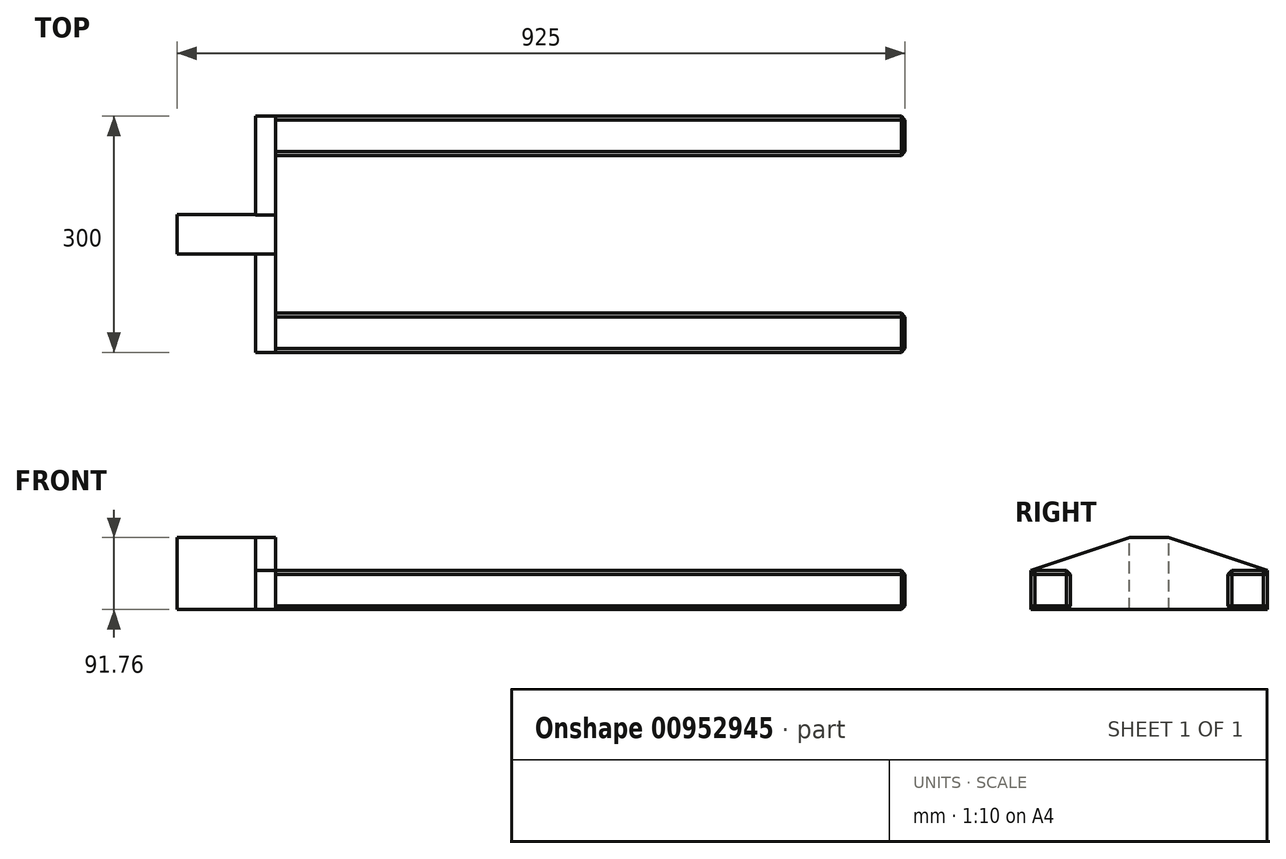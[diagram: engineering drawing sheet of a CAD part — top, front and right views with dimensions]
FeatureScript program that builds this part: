
annotation { "Feature Type Name" : "Feature", "Feature Type Description" : "" }
export const myFeature = defineFeature(function(context is Context, id is Id, definition is map)
    precondition{}
    {
        {
            var Q0;
            Q0=qCreatedBy(makeId("Top.planeOp"),FACE);
            var sketch = newSketch(context, id + "F0", { "sketchPlane" : qUnion([Q0])});
            skLineSegment(sketch, "E0.bottom", {"start": v(0, -100) * mm, "end": v(800, -100) * mm});
            skLineSegment(sketch, "E0.top", {"start": v(0, -150) * mm, "end": v(800, -150) * mm});
            skLineSegment(sketch, "E0.left", {"start": v(0, -100) * mm, "end": v(0, -150) * mm});
            skLineSegment(sketch, "E0.right", {"start": v(800, -100) * mm, "end": v(800, -150) * mm});
            skLineSegment(sketch, "E1.MirrorCS", {"start": v(0, 100) * mm, "end": v(800, 100) * mm});
            skLineSegment(sketch, "E2.MirrorCS", {"start": v(0, 100) * mm, "end": v(0, 150) * mm});
            skLineSegment(sketch, "E3.MirrorCS", {"start": v(0, 150) * mm, "end": v(800, 150) * mm});
            skLineSegment(sketch, "E4.MirrorCS", {"start": v(800, 100) * mm, "end": v(800, 150) * mm});
            skSolve(sketch);
        }
        {
            var Q0;
            Q0 = qSketchRegion(id + "F0", true);
            extrude(context, id + "F1", {"entities" : qUnion([Q0]), "depth" : 50 * mm, "offsetDistance" : 25 * mm});
        }
        {
            var Q0;
            Q0=makeQuery(id+"F1.opExtrude","SWEPT_FACE",FACE,{"disambiguationData":[OSD([sQuery(id+"F0.wireOp",EDGE,"E2.MirrorCS")])]});
            var sketch = newSketch(context, id + "F2", { "sketchPlane" : qUnion([Q0])});
            skLineSegment(sketch, "E5", {"start": v(0, 0) * mm, "end": v(-150, 0) * mm});
            skLineSegment(sketch, "E6", {"start": v(-150, 0) * mm, "end": v(-150, 50) * mm});
            skLineSegment(sketch, "E7", {"start": v(-150, 50) * mm, "end": v(-24.72, 91.76) * mm});
            skLineSegment(sketch, "E8", {"start": v(-24.72, 91.76) * mm, "end": v(0, 91.76) * mm});
            skLineSegment(sketch, "E9.MirrorCS", {"start": v(24.72, 91.76) * mm, "end": v(0, 91.76) * mm});
            skLineSegment(sketch, "E10.MirrorCS", {"start": v(150, 50) * mm, "end": v(24.72, 91.76) * mm});
            skLineSegment(sketch, "E11.MirrorCS", {"start": v(150, 0) * mm, "end": v(150, 50) * mm});
            skLineSegment(sketch, "E12.MirrorCS", {"start": v(0, 0) * mm, "end": v(150, 0) * mm});
            skSolve(sketch);
        }
        {
            var Q0;
            Q0=makeQuery(id+"F2.imprint","IMPRINT",FACE,{"disambiguationData":[TD([[makeQuery(id+"F2.imprint","IMPRINT",EDGE,{"derivedFrom":sQuery(id+"F2.wireOp",EDGE,"E7")}),-1.0]])]});
            var Q1;
            {var subQ3=sQuery(id+"F2.wireOp",EDGE,"E6");Q1=makeQuery(id+"F2.imprint","IMPRINT",FACE,{"disambiguationData":[TD([[makeQuery(id+"F2.imprint","IMPRINT",EDGE,{"derivedFrom":subQ3}),1.0]])]});}
            extrude(context, id + "F3", {"entities" : qUnion([Q0, Q1]), "depth" : 25 * mm, "offsetDistance" : 25 * mm});
        }
        {
            var Q0;
            Q0=makeQuery(id+"F3.opExtrude","CAP_FACE",FACE,{"disambiguationData":[OSD([sQuery(id+"F2.wireOp",EDGE,"E5"),sQuery(id+"F2.wireOp",EDGE,"E6"),sQuery(id+"F2.wireOp",EDGE,"E7"),sQuery(id+"F2.wireOp",EDGE,"E8"),sQuery(id+"F2.wireOp",EDGE,"E9.MirrorCS"),sQuery(id+"F2.wireOp",EDGE,"E10.MirrorCS"),sQuery(id+"F2.wireOp",EDGE,"E11.MirrorCS"),sQuery(id+"F2.wireOp",EDGE,"E12.MirrorCS")])],"isStart":false});
            var sketch = newSketch(context, id + "F4", { "sketchPlane" : qUnion([Q0])});
            skLineSegment(sketch, "E13", {"start": v(0, 0) * mm, "end": v(25, 0) * mm});
            skLineSegment(sketch, "E14", {"start": v(25, 0) * mm, "end": v(25, 91.76) * mm});
            skLineSegment(sketch, "E15", {"start": v(25, 91.76) * mm, "end": v(0, 91.76) * mm});
            skLineSegment(sketch, "E16.MirrorCS", {"start": v(-25, 91.76) * mm, "end": v(0, 91.76) * mm});
            skLineSegment(sketch, "E17.MirrorCS", {"start": v(-25, 0) * mm, "end": v(-25, 91.76) * mm});
            skLineSegment(sketch, "E18.MirrorCS", {"start": v(0, 0) * mm, "end": v(-25, 0) * mm});
            skSolve(sketch);
        }
        {
            var Q0;
            {var subQ0=sQuery(id+"F4.wireOp",EDGE,"E16.MirrorCS");var subQ3=sQuery(id+"F4.wireOp",EDGE,"E17.MirrorCS");var subQ4=makeQuery(id+"F4.imprint","INTERSECT",VERTEX,{"derivedFrom":[subQ0,subQ3]});Q0=makeQuery(id+"F4.imprint","IMPRINT",FACE,{"disambiguationData":[TD([[makeQuery(id+"F4.imprint","IMPRINT",EDGE,{"disambiguationData":[TD([[subQ4,-1.0]])],"derivedFrom":subQ0}),-1.0]])]});}
            var Q1;
            {var subQ11=sQuery(id+"F4.wireOp",EDGE,"E13");Q1=makeQuery(id+"F4.imprint","IMPRINT",FACE,{"disambiguationData":[TD([[makeQuery(id+"F4.imprint","IMPRINT",EDGE,{"derivedFrom":subQ11}),-1.0]])]});}
            var Q2;
            {var subQ0=sQuery(id+"F4.wireOp",EDGE,"E15");var subQ1=sQuery(id+"F4.wireOp",EDGE,"E14");var subQ2=makeQuery(id+"F4.imprint","INTERSECT",VERTEX,{"derivedFrom":[subQ1,subQ0]});Q2=makeQuery(id+"F4.imprint","IMPRINT",FACE,{"disambiguationData":[TD([[makeQuery(id+"F4.imprint","IMPRINT",EDGE,{"disambiguationData":[TD([[subQ2,1.0]])],"derivedFrom":subQ1}),1.0]])]});}
            extrude(context, id + "F5", {"entities" : qUnion([Q0, Q1, Q2]), "operationType" : NewBodyOperationType.ADD, "depth" : 100 * mm, "offsetDistance" : 25 * mm});
        }
        {
            var Q0;
            Q0=makeQuery(id+"F1.opExtrude","CAP_EDGE",EDGE,{"disambiguationData":[OSD([sQuery(id+"F0.wireOp",EDGE,"E1.MirrorCS")])],"isStart":false});
            var Q1;
            Q1=makeQuery(id+"F1.opExtrude","CAP_EDGE",EDGE,{"disambiguationData":[OSD([sQuery(id+"F0.wireOp",EDGE,"E0.bottom")])],"isStart":false});
            var Q2;
            Q2=makeQuery(id+"F1.opExtrude","CAP_EDGE",EDGE,{"disambiguationData":[OSD([sQuery(id+"F0.wireOp",EDGE,"E0.right")])],"isStart":false});
            var Q3;
            Q3=makeQuery(id+"F1.opExtrude","CAP_EDGE",EDGE,{"disambiguationData":[OSD([sQuery(id+"F0.wireOp",EDGE,"E4.MirrorCS")])],"isStart":false});
            var Q4;
            Q4=makeQuery(id+"F1.opExtrude","CAP_EDGE",EDGE,{"disambiguationData":[OSD([sQuery(id+"F0.wireOp",EDGE,"E0.top")])],"isStart":false});
            var Q5;
            Q5=makeQuery(id+"F1.opExtrude","CAP_EDGE",EDGE,{"disambiguationData":[OSD([sQuery(id+"F0.wireOp",EDGE,"E3.MirrorCS")])],"isStart":false});
            var Q6;
            Q6=makeQuery(id+"F1.opExtrude","SWEPT_EDGE",EDGE,{"disambiguationData":[OSD([sQuery(id+"F0.wireOp",EDGE,"E0.top"),sQuery(id+"F0.wireOp",EDGE,"E0.right")])]});
            var Q7;
            Q7=makeQuery(id+"F1.opExtrude","SWEPT_EDGE",EDGE,{"disambiguationData":[OSD([sQuery(id+"F0.wireOp",EDGE,"E0.bottom"),sQuery(id+"F0.wireOp",EDGE,"E0.right")])]});
            var Q8;
            Q8=makeQuery(id+"F1.opExtrude","SWEPT_EDGE",EDGE,{"disambiguationData":[OSD([sQuery(id+"F0.wireOp",EDGE,"E1.MirrorCS"),sQuery(id+"F0.wireOp",EDGE,"E4.MirrorCS")])]});
            var Q9;
            Q9=makeQuery(id+"F1.opExtrude","SWEPT_EDGE",EDGE,{"disambiguationData":[OSD([sQuery(id+"F0.wireOp",EDGE,"E3.MirrorCS"),sQuery(id+"F0.wireOp",EDGE,"E4.MirrorCS")])]});
            var Q10;
            Q10=makeQuery(id+"F1.opExtrude","CAP_EDGE",EDGE,{"disambiguationData":[OSD([sQuery(id+"F0.wireOp",EDGE,"E1.MirrorCS")])],"isStart":true});
            var Q11;
            Q11=makeQuery(id+"F1.opExtrude","CAP_EDGE",EDGE,{"disambiguationData":[OSD([sQuery(id+"F0.wireOp",EDGE,"E0.top")])],"isStart":true});
            var Q12;
            Q12=makeQuery(id+"F1.opExtrude","CAP_EDGE",EDGE,{"disambiguationData":[OSD([sQuery(id+"F0.wireOp",EDGE,"E0.bottom")])],"isStart":true});
            var Q13;
            Q13=makeQuery(id+"F1.opExtrude","CAP_EDGE",EDGE,{"disambiguationData":[OSD([sQuery(id+"F0.wireOp",EDGE,"E3.MirrorCS")])],"isStart":true});
            var Q14;
            Q14=makeQuery(id+"F1.opExtrude","CAP_EDGE",EDGE,{"disambiguationData":[OSD([sQuery(id+"F0.wireOp",EDGE,"E4.MirrorCS")])],"isStart":true});
            var Q15;
            Q15=makeQuery(id+"F1.opExtrude","CAP_EDGE",EDGE,{"disambiguationData":[OSD([sQuery(id+"F0.wireOp",EDGE,"E0.right")])],"isStart":true});
            chamfer(context, id + "F6", {"entities" : qUnion([Q0, Q1, Q2, Q3, Q4, Q5, Q6, Q7, Q8, Q9, Q10, Q11, Q12, Q13, Q14, Q15]), "width" : 5 * mm, "tangentPropagation" : true});
        }
    });
